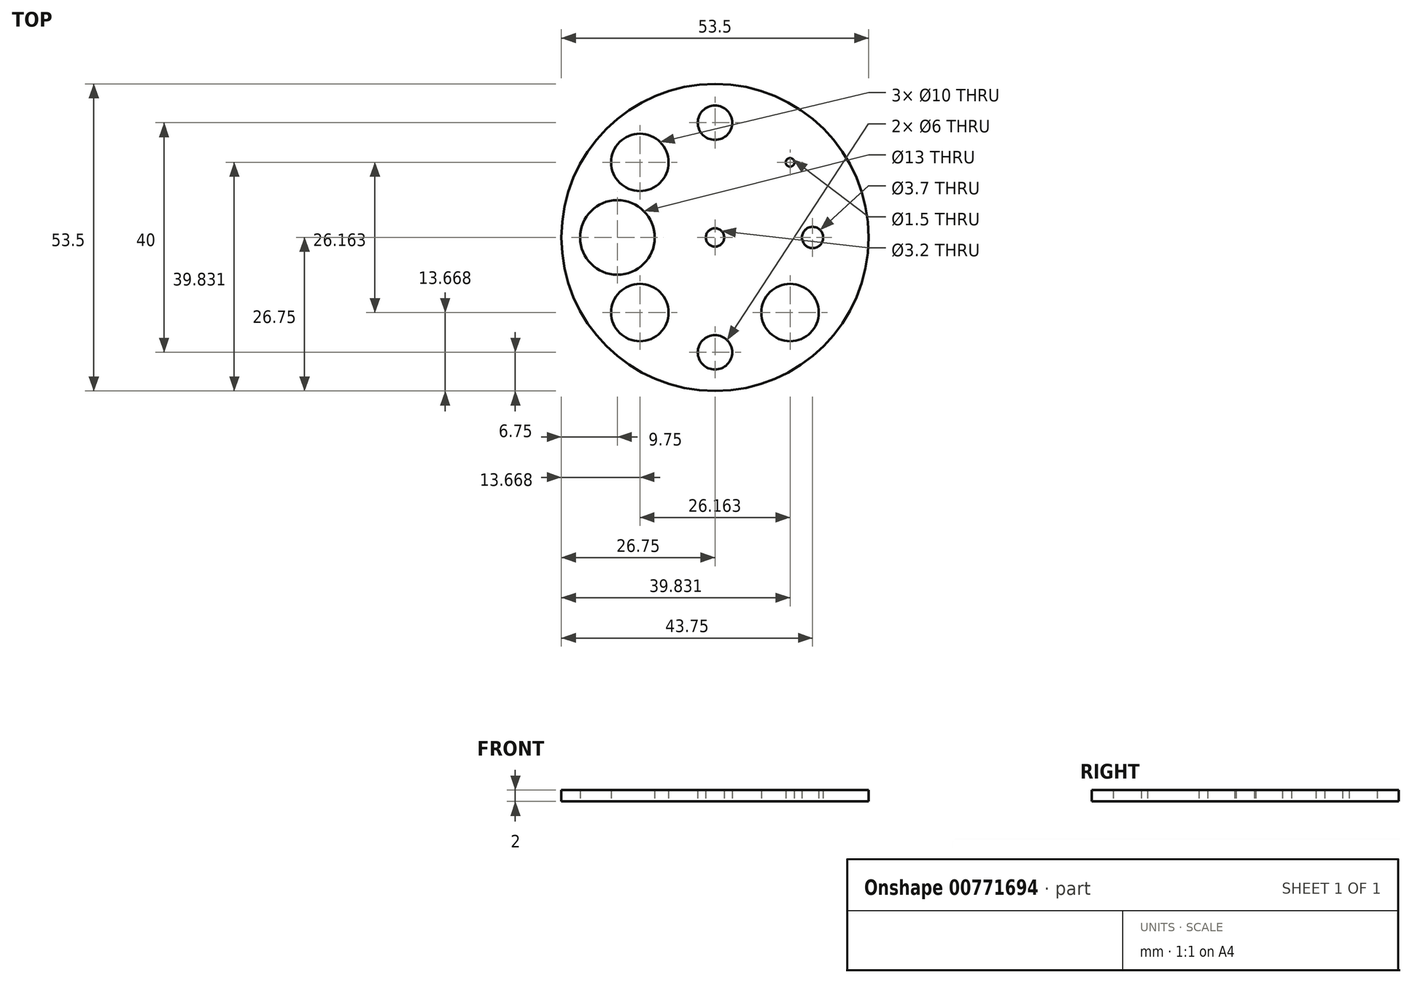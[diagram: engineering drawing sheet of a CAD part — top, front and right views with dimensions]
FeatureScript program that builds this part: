
annotation { "Feature Type Name" : "Feature", "Feature Type Description" : "" }
export const myFeature = defineFeature(function(context is Context, id is Id, definition is map)
    precondition{}
    {
        {
            var Q0;
            Q0=qCreatedBy(makeId("Top.planeOp"),FACE);
            var sketch = newSketch(context, id + "F0", { "sketchPlane" : qUnion([Q0])});
            skCircle(sketch, "E0", {"center": v(0, 0) * mm, "radius": 26.75 * mm});
            skLineSegment(sketch, "E1.bottom", {"start": v(13.08, 13.08) * mm, "end": v(-13.08, 13.08) * mm});
            skLineSegment(sketch, "E1.top", {"start": v(13.08, -13.08) * mm, "end": v(-13.08, -13.08) * mm});
            skLineSegment(sketch, "E1.left", {"start": v(13.08, 13.08) * mm, "end": v(13.08, -13.08) * mm});
            skLineSegment(sketch, "E1.right", {"start": v(-13.08, 13.08) * mm, "end": v(-13.08, -13.08) * mm});
            skCircle(sketch, "E2", {"center": v(-13.08, 13.08) * mm, "radius": 5 * mm});
            skCircle(sketch, "E3", {"center": v(-13.08, -13.08) * mm, "radius": 5 * mm});
            skCircle(sketch, "E4", {"center": v(13.08, -13.08) * mm, "radius": 5 * mm});
            skPoint(sketch, "E5", {"position": v(0, -20) * mm});
            skPoint(sketch, "E6", {"position": v(0, 20) * mm});
            skCircle(sketch, "E7", {"center": v(0, 20) * mm, "radius": 3 * mm});
            skCircle(sketch, "E8", {"center": v(0, -20) * mm, "radius": 3 * mm});
            skCircle(sketch, "E9", {"center": v(-17, 0) * mm, "radius": 6.5 * mm});
            skCircle(sketch, "E10", {"center": v(17, 0) * mm, "radius": 1.85 * mm});
            skCircle(sketch, "E11", {"center": v(0, 0) * mm, "radius": 1.6 * mm});
            skCircle(sketch, "E12", {"center": v(13.08, 13.08) * mm, "radius": 0.75 * mm});
            skSolve(sketch);
        }
        {
            var Q0;
            Q0 = qSketchRegion(id + "F0", true);
            var Q1;
            Q1=makeQuery(id+"F0.imprint","IMPRINT",FACE,{"disambiguationData":[TD([[makeQuery(id+"F0.imprint","IMPRINT",EDGE,{"derivedFrom":sQuery(id+"F0.wireOp",EDGE,"E11")}),-1.0]])]});
            extrude(context, id + "F1", {"entities" : qUnion([Q0, Q1]), "depth" : 2 * mm, "offsetDistance" : 25 * mm});
        }
    });
